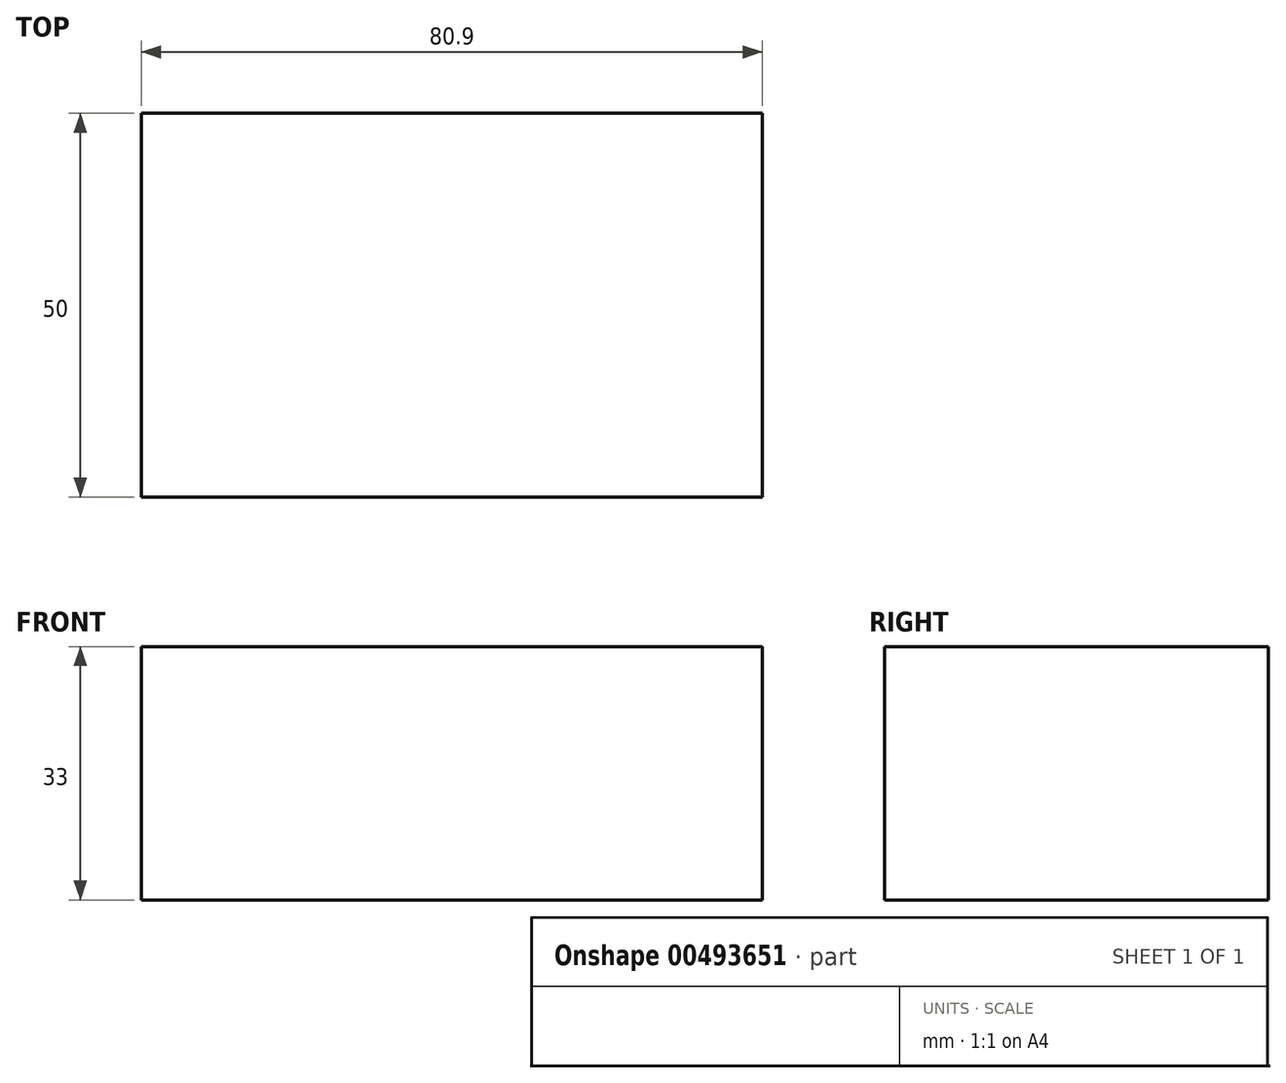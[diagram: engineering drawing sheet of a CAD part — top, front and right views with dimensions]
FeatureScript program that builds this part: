
annotation { "Feature Type Name" : "Feature", "Feature Type Description" : "" }
export const myFeature = defineFeature(function(context is Context, id is Id, definition is map)
    precondition{}
    {
        {
            var Q0;
            Q0=qCreatedBy(makeId("Front.planeOp"),FACE);
            var sketch = newSketch(context, id + "F0", { "sketchPlane" : qUnion([Q0])});
            skLineSegment(sketch, "E0.bottom", {"start": v(40.45, 16.5) * mm, "end": v(-40.45, 16.5) * mm});
            skLineSegment(sketch, "E0.top", {"start": v(40.45, -16.5) * mm, "end": v(-40.45, -16.5) * mm});
            skLineSegment(sketch, "E0.left", {"start": v(40.45, 16.5) * mm, "end": v(40.45, -16.5) * mm});
            skLineSegment(sketch, "E0.right", {"start": v(-40.45, 16.5) * mm, "end": v(-40.45, -16.5) * mm});
            skPoint(sketch, "E0.middle", {"position": v(0, 0) * mm});
            skSolve(sketch);
        }
        {
            var Q0;
            Q0=makeQuery(id+"F0.imprint","IMPRINT",FACE,{"disambiguationData":[TD([[makeQuery(id+"F0.imprint","IMPRINT",EDGE,{"derivedFrom":sQuery(id+"F0.wireOp",EDGE,"E0.bottom")}),1.0]])]});
            extrude(context, id + "F1", {"entities" : qUnion([Q0]), "depth" : 50 * mm});
        }
    });
